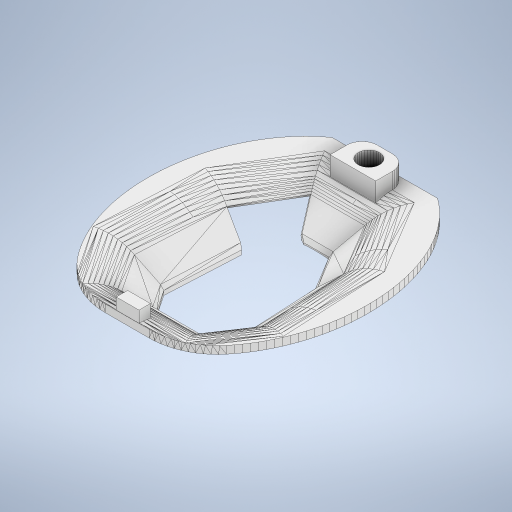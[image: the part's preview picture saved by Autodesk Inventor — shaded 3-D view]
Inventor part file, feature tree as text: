
AUTODESK INVENTOR PART (.ipt)
format: ipt  version: 2023.5 (Build 275446000, 446)  size: 1,057,792 bytes
history: native  units: in
note: dims shown in document units (in); Inventor stores cm internally (conversion verified against a paired STEP export)
features: extrude x3, sketch x3, other x2
ambient origin geometry x8: Origin, YZ Plane, XZ Plane, XY Plane, X Axis, Y Axis, Z Axis, Center Point
bodies: Solid1 (feature_tree)
feature tree (8):
  other  "rat_cap_base_v8"
  other  "MeshFeature1"
  extrude  "Extrusion1"  TaperAngle=0.0deg  [1 undecoded]
  extrude  "Extrusion2"  [1 undecoded]
  extrude  "Extrusion3"  [1 undecoded]
  sketch  "Sketch1"  dims[d0=0.0in d1=0.0in d2=0.0in d3=0.0in]
  sketch  "Sketch2"  dims[d4=0.0in d5=0.0in]
  sketch  "Sketch3"
note: 3 required parameter values undecoded (feature->parameter linkage not recoverable at this tier; creation-order binding heuristic only, values carry confidence <= 0.55)
